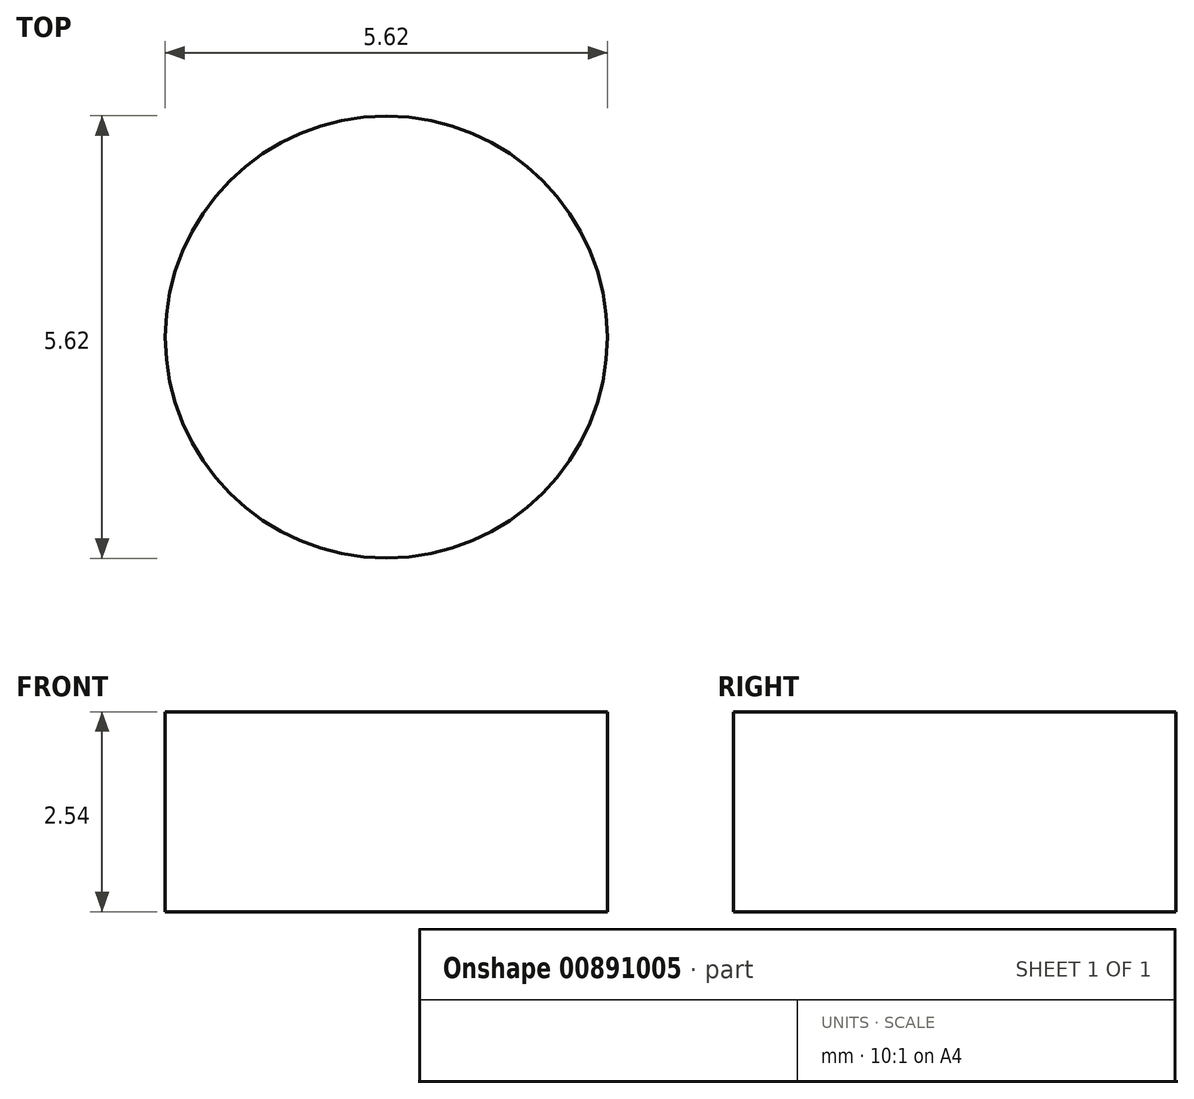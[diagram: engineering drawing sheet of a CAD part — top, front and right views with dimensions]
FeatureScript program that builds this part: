
annotation { "Feature Type Name" : "Feature", "Feature Type Description" : "" }
export const myFeature = defineFeature(function(context is Context, id is Id, definition is map)
    precondition{}
    {
        {
            var Q0;
            Q0=qCreatedBy(makeId("Top.planeOp"),FACE);
            var sketch = newSketch(context, id + "F0", { "sketchPlane" : qUnion([Q0])});
            skCircle(sketch, "E0", {"center": v(0, 0) * mm, "radius": 2.8 * mm});
            skSolve(sketch);
        }
        {
            var Q0;
            Q0 = qSketchRegion(id + "F0", true);
            extrude(context, id + "F1", {"entities" : qUnion([Q0]), "depth" : 2.54 * mm, "offsetDistance" : 25.4 * mm});
        }
    });
